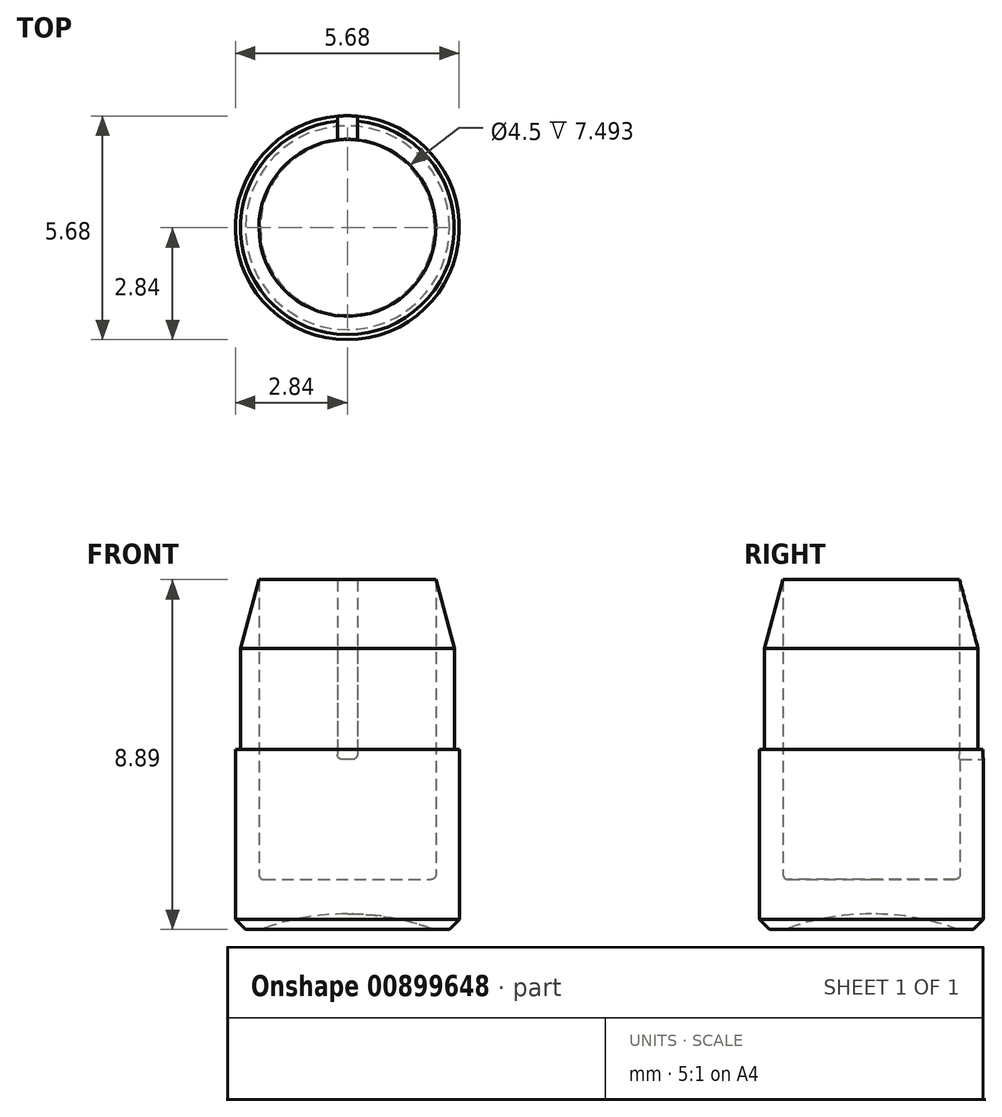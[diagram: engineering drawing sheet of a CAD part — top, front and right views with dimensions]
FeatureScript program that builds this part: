
annotation { "Feature Type Name" : "Feature", "Feature Type Description" : "" }
export const myFeature = defineFeature(function(context is Context, id is Id, definition is map)
    precondition{}
    {
        {
            var Q0;
            Q0=qCreatedBy(makeId("Front.planeOp"),FACE);
            var sketch = newSketch(context, id + "F0", { "sketchPlane" : qUnion([Q0])});
            skLineSegment(sketch, "E0", {"start": v(2.84, 0) * mm, "end": v(2.84, 4.57) * mm});
            skLineSegment(sketch, "E1", {"start": v(2.72, 7.14) * mm, "end": v(2.25, 8.89) * mm});
            skLineSegment(sketch, "E2", {"start": v(2.25, 8.9) * mm, "end": v(2.25, 1.4) * mm});
            skLineSegment(sketch, "E3", {"start": v(2.12, 1.27) * mm, "end": v(0, 1.27) * mm});
            skLineSegment(sketch, "E4", {"start": v(2.84, 0) * mm, "end": v(2.2, 0) * mm});
            skLineSegment(sketch, "E5.MirrorCS", {"start": v(-2.84, 6.66) * mm, "end": v(-2.25, 8.9) * mm, "construction": true});
            skLineSegment(sketch, "E6.MirrorCS", {"start": v(-2.84, 0) * mm, "end": v(-2.84, 6.66) * mm, "construction": true});
            skLineSegment(sketch, "E7.MirrorCS", {"start": v(-2.25, 8.9) * mm, "end": v(-2.25, 1.27) * mm, "construction": true});
            skLineSegment(sketch, "E8.MirrorCS", {"start": v(-2.25, 1.27) * mm, "end": v(0, 1.27) * mm, "construction": true});
            skLineSegment(sketch, "E9.MirrorCS", {"start": v(-2.84, 0) * mm, "end": v(0, 0) * mm, "construction": true});
            skLineSegment(sketch, "E10.MirrorCS", {"start": v(-2.25, 8.9) * mm, "end": v(-2.25, 1.27) * mm});
            skLineSegment(sketch, "E11", {"start": v(0, 1.69) * mm, "end": v(0, 13.44) * mm, "construction": true});
            skLineSegment(sketch, "E12", {"start": v(0, 1.27) * mm, "end": v(0, 0.4) * mm});
            skPoint(sketch, "E13.visualSharp", {"position": v(2.25, 1.27) * mm});
            skArc(sketch, "E13.filletArc", {"start": v(2.12, 1.27) * mm, "mid": v(2.21, 1.3) * mm, "end": v(2.25, 1.4) * mm});
            skLineSegment(sketch, "E14", {"start": v(2.84, 4.57) * mm, "end": v(2.72, 4.57) * mm});
            skLineSegment(sketch, "E15", {"start": v(2.72, 4.57) * mm, "end": v(2.72, 7.14) * mm});
            skPoint(sketch, "E16.orphan", {"position": v(2.84, 6.66) * mm});
            skArc(sketch, "E17", {"start": v(2.2, 0) * mm, "mid": v(1.12, 0.3) * mm, "end": v(0, 0.4) * mm});
            skPoint(sketch, "E18.orphan", {"position": v(0, 0) * mm});
            skArc(sketch, "E19", {"start": v(0, 0.4) * mm, "mid": v(-1.12, 0.3) * mm, "end": v(-2.2, 0) * mm, "construction": true});
            skSolve(sketch);
        }
        {
            var Q0;
            Q0 = qSketchRegion(id + "F0", true);
            var Q1;
            Q1=sQuery(id+"F0.wireOp",EDGE,"E11");
            revolve(context, id + "F1", {"surfaceOperationType" : NewSurfaceOperationType.NEW, "entities" : qUnion([Q0]), "axis" : qUnion([Q1]), "revolveType" : RevolveType.FULL});
        }
        {
            var Q0;
            Q0=qCreatedBy(makeId("Top.planeOp"),FACE);
            cPlane(context, id + "F2", {"entities" : qUnion([Q0]), "cplaneType" : CPlaneType.OFFSET, "offset" : 8.9 * mm, "width" : 152.4 * mm, "height" : 152.4 * mm});
        }
        {
            var Q0;
            Q0=makeQuery(id+"F1.opRevolve","SWEPT_EDGE",EDGE,{"disambiguationData":[OSD([sQuery(id+"F0.wireOp",EDGE,"E0"),sQuery(id+"F0.wireOp",EDGE,"E4")])]});
            chamfer(context, id + "F3", {"entities" : qUnion([Q0]), "width" : 0.25 * mm, "tangentPropagation" : true});
        }
        {
            var Q0;
            Q0=qCreatedBy(id+"F2.planeOp",FACE);
            var sketch = newSketch(context, id + "F4", { "sketchPlane" : qUnion([Q0])});
            skLineSegment(sketch, "E20.bottom", {"start": v(-0.25, 0) * mm, "end": v(0.25, 0) * mm});
            skLineSegment(sketch, "E20.top", {"start": v(-0.25, 3.05) * mm, "end": v(0.25, 3.05) * mm});
            skLineSegment(sketch, "E20.left", {"start": v(-0.25, 0) * mm, "end": v(-0.25, 3.05) * mm});
            skLineSegment(sketch, "E20.right", {"start": v(0.25, 0) * mm, "end": v(0.25, 3.05) * mm});
            skSolve(sketch);
        }
        {
            var Q0;
            Q0=qCreatedBy(makeId("Front.planeOp"),FACE);
            var sketch = newSketch(context, id + "F5", { "sketchPlane" : qUnion([Q0])});
            skLineSegment(sketch, "E21", {"start": v(0, 0) * mm, "end": v(0, 8.89) * mm});
            skSolve(sketch);
        }
        {
            var Q0;
            Q0 = qSketchRegion(id + "F4", true);
            extrude(context, id + "F6", {"entities" : qUnion([Q0]), "operationType" : NewBodyOperationType.REMOVE, "oppositeDirection" : true, "depth" : 4.57 * mm, "offsetDistance" : 25.4 * mm});
        }
        {
            var Q0;
            Q0=makeQuery(id+"F6.boolean.opBoolean","COPY",EDGE,{"derivedFrom":makeQuery(id+"F6.opExtrude","CAP_EDGE",EDGE,{"disambiguationData":[OSD([sQuery(id+"F4.wireOp",EDGE,"E20.left")])],"isStart":false})});
            var Q1;
            Q1=makeQuery(id+"F6.boolean.opBoolean","COPY",EDGE,{"derivedFrom":makeQuery(id+"F6.opExtrude","CAP_EDGE",EDGE,{"disambiguationData":[OSD([sQuery(id+"F4.wireOp",EDGE,"E20.right")])],"isStart":false})});
            var Q2;
            Q2=makeQuery(id+"FYxwC5J9NQOt40T_1.1.F6.boolean.opBoolean","COPY",EDGE,{"derivedFrom":makeQuery(id+"FYxwC5J9NQOt40T_1.1.F6.opExtrude","CAP_EDGE",EDGE,{"disambiguationData":[OSD([sQuery(id+"F4.wireOp",EDGE,"E20.left")])],"isStart":false})});
            var Q3;
            Q3=makeQuery(id+"FYxwC5J9NQOt40T_1.1.F6.boolean.opBoolean","COPY",EDGE,{"derivedFrom":makeQuery(id+"FYxwC5J9NQOt40T_1.1.F6.opExtrude","CAP_EDGE",EDGE,{"disambiguationData":[OSD([sQuery(id+"F4.wireOp",EDGE,"E20.right")])],"isStart":false})});
            var Q4;
            Q4=makeQuery(id+"FYxwC5J9NQOt40T_1.5.F6.boolean.opBoolean","COPY",EDGE,{"derivedFrom":makeQuery(id+"FYxwC5J9NQOt40T_1.5.F6.opExtrude","CAP_EDGE",EDGE,{"disambiguationData":[OSD([sQuery(id+"F4.wireOp",EDGE,"E20.left")])],"isStart":false})});
            var Q5;
            Q5=makeQuery(id+"FYxwC5J9NQOt40T_1.5.F6.boolean.opBoolean","COPY",EDGE,{"derivedFrom":makeQuery(id+"FYxwC5J9NQOt40T_1.5.F6.opExtrude","CAP_EDGE",EDGE,{"disambiguationData":[OSD([sQuery(id+"F4.wireOp",EDGE,"E20.right")])],"isStart":false})});
            var Q6;
            Q6=makeQuery(id+"FYxwC5J9NQOt40T_1.4.F6.boolean.opBoolean","COPY",EDGE,{"derivedFrom":makeQuery(id+"FYxwC5J9NQOt40T_1.4.F6.opExtrude","CAP_EDGE",EDGE,{"disambiguationData":[OSD([sQuery(id+"F4.wireOp",EDGE,"E20.left")])],"isStart":false})});
            var Q7;
            Q7=makeQuery(id+"FYxwC5J9NQOt40T_1.4.F6.boolean.opBoolean","COPY",EDGE,{"derivedFrom":makeQuery(id+"FYxwC5J9NQOt40T_1.4.F6.opExtrude","CAP_EDGE",EDGE,{"disambiguationData":[OSD([sQuery(id+"F4.wireOp",EDGE,"E20.right")])],"isStart":false})});
            var Q8;
            Q8=makeQuery(id+"FYxwC5J9NQOt40T_1.3.F6.boolean.opBoolean","COPY",EDGE,{"derivedFrom":makeQuery(id+"FYxwC5J9NQOt40T_1.3.F6.opExtrude","CAP_EDGE",EDGE,{"disambiguationData":[OSD([sQuery(id+"F4.wireOp",EDGE,"E20.left")])],"isStart":false})});
            var Q9;
            Q9=makeQuery(id+"FYxwC5J9NQOt40T_1.3.F6.boolean.opBoolean","COPY",EDGE,{"derivedFrom":makeQuery(id+"FYxwC5J9NQOt40T_1.3.F6.opExtrude","CAP_EDGE",EDGE,{"disambiguationData":[OSD([sQuery(id+"F4.wireOp",EDGE,"E20.right")])],"isStart":false})});
            var Q10;
            Q10=makeQuery(id+"FYxwC5J9NQOt40T_1.2.F6.boolean.opBoolean","COPY",EDGE,{"derivedFrom":makeQuery(id+"FYxwC5J9NQOt40T_1.2.F6.opExtrude","CAP_EDGE",EDGE,{"disambiguationData":[OSD([sQuery(id+"F4.wireOp",EDGE,"E20.left")])],"isStart":false})});
            var Q11;
            Q11=makeQuery(id+"FYxwC5J9NQOt40T_1.2.F6.boolean.opBoolean","COPY",EDGE,{"derivedFrom":makeQuery(id+"FYxwC5J9NQOt40T_1.2.F6.opExtrude","CAP_EDGE",EDGE,{"disambiguationData":[OSD([sQuery(id+"F4.wireOp",EDGE,"E20.right")])],"isStart":false})});
            fillet(context, id + "F7", {"entities" : qUnion([Q0, Q1, Q2, Q3, Q4, Q5, Q6, Q7, Q8, Q9, Q10, Q11]), "radius" : 0.13 * mm, "tangentPropagation" : true, "allowEdgeOverflow" : false});
        }
        {
            var Q0;
            {var subQ0=sQuery(id+"F0.wireOp",EDGE,"E14");var subQ2=sQuery(id+"F0.wireOp",EDGE,"E15");var subQ4=makeQuery(id+"FYxwC5J9NQOt40T_1.1.F6.opExtrude","SWEPT_FACE",FACE,{"disambiguationData":[OSD([sQuery(id+"F4.wireOp",EDGE,"E20.left")])]});var subQ5=sQuery(id+"F4.wireOp",EDGE,"E20.right");Q0=makeQuery(id+"FYxwC5J9NQOt40T_1.2.F6.boolean.opBoolean","SPLIT",EDGE,{"disambiguationData":[TD([makeQuery(id+"FYxwC5J9NQOt40T_1.1.F6.boolean.opBoolean","COPY",FACE,{"derivedFrom":subQ4})])],"derivedFrom":makeQuery(id+"FYxwC5J9NQOt40T_1.1.F6.boolean.opBoolean","SPLIT",EDGE,{"disambiguationData":[TD([makeQuery(id+"F6.boolean.opBoolean","COPY",FACE,{"derivedFrom":makeQuery(id+"F6.opExtrude","SWEPT_FACE",FACE,{"disambiguationData":[OSD([subQ5])]})})])],"derivedFrom":makeQuery(id+"F1.opRevolve","SWEPT_EDGE",EDGE,{"disambiguationData":[OSD([subQ0,subQ2])]})})});}
            var Q1;
            {var subQ0=sQuery(id+"F0.wireOp",EDGE,"E14");var subQ2=sQuery(id+"F0.wireOp",EDGE,"E15");var subQ4=sQuery(id+"F4.wireOp",EDGE,"E20.left");var subQ5=makeQuery(id+"FYxwC5J9NQOt40T_1.2.F6.opExtrude","SWEPT_FACE",FACE,{"disambiguationData":[OSD([subQ4])]});var subQ6=sQuery(id+"F4.wireOp",EDGE,"E20.right");var subQ7=makeQuery(id+"F6.boolean.opBoolean","COPY",FACE,{"derivedFrom":makeQuery(id+"F6.opExtrude","SWEPT_FACE",FACE,{"disambiguationData":[OSD([subQ6])]})});Q1=makeQuery(id+"FYxwC5J9NQOt40T_1.3.F6.boolean.opBoolean","SPLIT",EDGE,{"disambiguationData":[TD([makeQuery(id+"FYxwC5J9NQOt40T_1.2.F6.boolean.opBoolean","COPY",FACE,{"derivedFrom":subQ5})])],"derivedFrom":makeQuery(id+"FYxwC5J9NQOt40T_1.2.F6.boolean.opBoolean","SPLIT",EDGE,{"disambiguationData":[TD([subQ7])],"derivedFrom":makeQuery(id+"FYxwC5J9NQOt40T_1.1.F6.boolean.opBoolean","SPLIT",EDGE,{"disambiguationData":[TD([subQ7])],"derivedFrom":makeQuery(id+"F1.opRevolve","SWEPT_EDGE",EDGE,{"disambiguationData":[OSD([subQ0,subQ2])]})})})});}
            var Q2;
            {var subQ0=sQuery(id+"F0.wireOp",EDGE,"E14");var subQ1=sQuery(id+"F0.wireOp",EDGE,"E15");Q2=makeQuery(id+"FYxwC5J9NQOt40T_1.1.F6.boolean.opBoolean","SPLIT",EDGE,{"disambiguationData":[TD([makeQuery(id+"F6.boolean.opBoolean","COPY",FACE,{"derivedFrom":makeQuery(id+"F6.opExtrude","SWEPT_FACE",FACE,{"disambiguationData":[OSD([sQuery(id+"F4.wireOp",EDGE,"E20.left")])]})})])],"derivedFrom":makeQuery(id+"F1.opRevolve","SWEPT_EDGE",EDGE,{"disambiguationData":[OSD([subQ0,subQ1])]})});}
            var Q3;
            {var subQ0=sQuery(id+"F0.wireOp",EDGE,"E14");var subQ2=sQuery(id+"F0.wireOp",EDGE,"E15");var subQ4=makeQuery(id+"F6.boolean.opBoolean","COPY",FACE,{"derivedFrom":makeQuery(id+"F6.opExtrude","SWEPT_FACE",FACE,{"disambiguationData":[OSD([sQuery(id+"F4.wireOp",EDGE,"E20.right")])]})});Q3=makeQuery(id+"FYxwC5J9NQOt40T_1.5.F6.boolean.opBoolean","SPLIT",EDGE,{"disambiguationData":[TD([subQ4])],"derivedFrom":makeQuery(id+"FYxwC5J9NQOt40T_1.4.F6.boolean.opBoolean","SPLIT",EDGE,{"disambiguationData":[TD([subQ4])],"derivedFrom":makeQuery(id+"FYxwC5J9NQOt40T_1.3.F6.boolean.opBoolean","SPLIT",EDGE,{"disambiguationData":[TD([subQ4])],"derivedFrom":makeQuery(id+"FYxwC5J9NQOt40T_1.2.F6.boolean.opBoolean","SPLIT",EDGE,{"disambiguationData":[TD([subQ4])],"derivedFrom":makeQuery(id+"FYxwC5J9NQOt40T_1.1.F6.boolean.opBoolean","SPLIT",EDGE,{"disambiguationData":[TD([subQ4])],"derivedFrom":makeQuery(id+"F1.opRevolve","SWEPT_EDGE",EDGE,{"disambiguationData":[OSD([subQ0,subQ2])]})})})})})});}
            var Q4;
            {var subQ0=sQuery(id+"F0.wireOp",EDGE,"E14");var subQ2=sQuery(id+"F0.wireOp",EDGE,"E15");var subQ4=sQuery(id+"F4.wireOp",EDGE,"E20.left");var subQ5=makeQuery(id+"FYxwC5J9NQOt40T_1.3.F6.opExtrude","SWEPT_FACE",FACE,{"disambiguationData":[OSD([subQ4])]});var subQ6=sQuery(id+"F4.wireOp",EDGE,"E20.right");var subQ7=makeQuery(id+"F6.boolean.opBoolean","COPY",FACE,{"derivedFrom":makeQuery(id+"F6.opExtrude","SWEPT_FACE",FACE,{"disambiguationData":[OSD([subQ6])]})});Q4=makeQuery(id+"FYxwC5J9NQOt40T_1.4.F6.boolean.opBoolean","SPLIT",EDGE,{"disambiguationData":[TD([makeQuery(id+"FYxwC5J9NQOt40T_1.3.F6.boolean.opBoolean","COPY",FACE,{"derivedFrom":subQ5})])],"derivedFrom":makeQuery(id+"FYxwC5J9NQOt40T_1.3.F6.boolean.opBoolean","SPLIT",EDGE,{"disambiguationData":[TD([subQ7])],"derivedFrom":makeQuery(id+"FYxwC5J9NQOt40T_1.2.F6.boolean.opBoolean","SPLIT",EDGE,{"disambiguationData":[TD([subQ7])],"derivedFrom":makeQuery(id+"FYxwC5J9NQOt40T_1.1.F6.boolean.opBoolean","SPLIT",EDGE,{"disambiguationData":[TD([subQ7])],"derivedFrom":makeQuery(id+"F1.opRevolve","SWEPT_EDGE",EDGE,{"disambiguationData":[OSD([subQ0,subQ2])]})})})})});}
            var Q5;
            {var subQ0=sQuery(id+"F0.wireOp",EDGE,"E14");var subQ2=sQuery(id+"F4.wireOp",EDGE,"E20.left");var subQ3=makeQuery(id+"FYxwC5J9NQOt40T_1.4.F6.opExtrude","SWEPT_FACE",FACE,{"disambiguationData":[OSD([subQ2])]});var subQ4=sQuery(id+"F4.wireOp",EDGE,"E20.right");var subQ5=sQuery(id+"F0.wireOp",EDGE,"E15");var subQ7=makeQuery(id+"F6.boolean.opBoolean","COPY",FACE,{"derivedFrom":makeQuery(id+"F6.opExtrude","SWEPT_FACE",FACE,{"disambiguationData":[OSD([subQ4])]})});Q5=makeQuery(id+"FYxwC5J9NQOt40T_1.5.F6.boolean.opBoolean","SPLIT",EDGE,{"disambiguationData":[TD([makeQuery(id+"FYxwC5J9NQOt40T_1.4.F6.boolean.opBoolean","COPY",FACE,{"derivedFrom":subQ3})])],"derivedFrom":makeQuery(id+"FYxwC5J9NQOt40T_1.4.F6.boolean.opBoolean","SPLIT",EDGE,{"disambiguationData":[TD([subQ7])],"derivedFrom":makeQuery(id+"FYxwC5J9NQOt40T_1.3.F6.boolean.opBoolean","SPLIT",EDGE,{"disambiguationData":[TD([subQ7])],"derivedFrom":makeQuery(id+"FYxwC5J9NQOt40T_1.2.F6.boolean.opBoolean","SPLIT",EDGE,{"disambiguationData":[TD([subQ7])],"derivedFrom":makeQuery(id+"FYxwC5J9NQOt40T_1.1.F6.boolean.opBoolean","SPLIT",EDGE,{"disambiguationData":[TD([subQ7])],"derivedFrom":makeQuery(id+"F1.opRevolve","SWEPT_EDGE",EDGE,{"disambiguationData":[OSD([subQ0,subQ5])]})})})})})});}
            fillet(context, id + "F8", {"entities" : qUnion([Q0, Q1, Q2, Q3, Q4, Q5]), "radius" : 0.05 * mm, "tangentPropagation" : true, "allowEdgeOverflow" : false});
        }
    });
